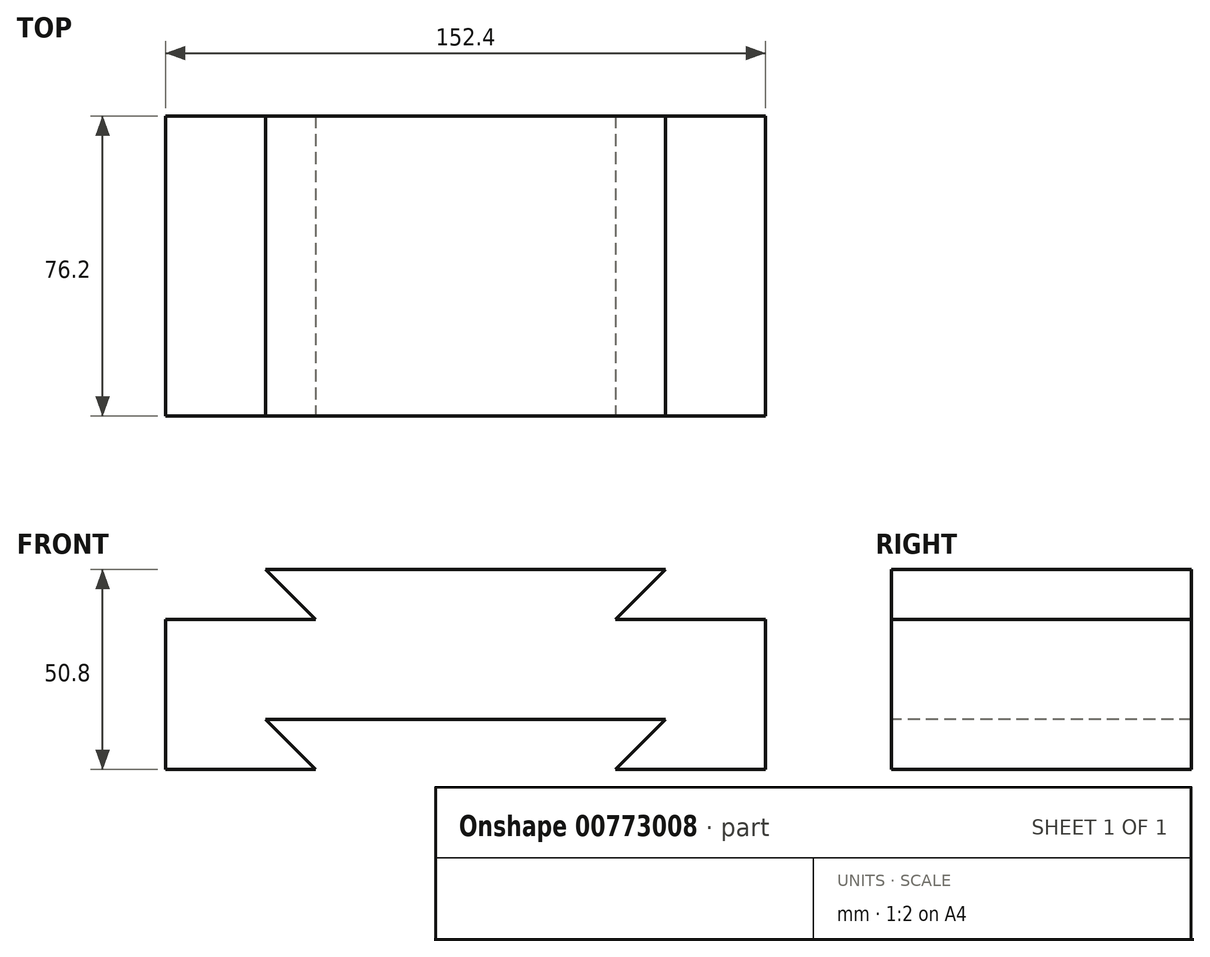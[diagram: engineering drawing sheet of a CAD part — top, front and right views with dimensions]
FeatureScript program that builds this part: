
annotation { "Feature Type Name" : "Feature", "Feature Type Description" : "" }
export const myFeature = defineFeature(function(context is Context, id is Id, definition is map)
    precondition{}
    {
        {
            var Q0;
            Q0=qCreatedBy(makeId("Front.planeOp"),FACE);
            var sketch = newSketch(context, id + "F0", { "sketchPlane" : qUnion([Q0])});
            skLineSegment(sketch, "E0", {"start": v(0, 0) * mm, "end": v(152.4, 0) * mm});
            skLineSegment(sketch, "E1", {"start": v(152.4, 0) * mm, "end": v(152.4, 50.8) * mm});
            skLineSegment(sketch, "E2", {"start": v(152.4, 50.8) * mm, "end": v(0, 50.8) * mm});
            skLineSegment(sketch, "E3", {"start": v(0, 50.8) * mm, "end": v(0, 0) * mm});
            skSolve(sketch);
        }
        {
            var Q0;
            Q0=makeQuery(id+"F0.imprint","IMPRINT",FACE,{"disambiguationData":[TD([[makeQuery(id+"F0.imprint","IMPRINT",EDGE,{"derivedFrom":sQuery(id+"F0.wireOp",EDGE,"E0")}),1.0]])]});
            extrude(context, id + "F1", {"entities" : qUnion([Q0]), "depth" : 76.2 * mm, "offsetDistance" : 25.4 * mm});
        }
        {
            var Q0;
            Q0=makeQuery(id+"F1.opExtrude","CAP_FACE",FACE,{"disambiguationData":[OSD([sQuery(id+"F0.wireOp",EDGE,"E0"),sQuery(id+"F0.wireOp",EDGE,"E1"),sQuery(id+"F0.wireOp",EDGE,"E2"),sQuery(id+"F0.wireOp",EDGE,"E3")])],"isStart":false});
            var sketch = newSketch(context, id + "F2", { "sketchPlane" : qUnion([Q0])});
            skLineSegment(sketch, "E4", {"start": v(0, 50.8) * mm, "end": v(25.4, 50.8) * mm});
            skLineSegment(sketch, "E5", {"start": v(0, 50.8) * mm, "end": v(0, 38.1) * mm});
            skLineSegment(sketch, "E6", {"start": v(0, 38.1) * mm, "end": v(38.1, 38.1) * mm});
            skLineSegment(sketch, "E7", {"start": v(25.4, 50.8) * mm, "end": v(38.1, 38.1) * mm});
            skSolve(sketch);
        }
        {
            var Q0;
            Q0=makeQuery(id+"F2.imprint","IMPRINT",FACE,{"disambiguationData":[TD([[makeQuery(id+"F2.imprint","IMPRINT",EDGE,{"derivedFrom":sQuery(id+"F2.wireOp",EDGE,"E4")}),1.0]])]});
            extrude(context, id + "F3", {"entities" : qUnion([Q0]), "operationType" : NewBodyOperationType.REMOVE, "oppositeDirection" : true, "depth" : 76.2 * mm, "offsetDistance" : 25.4 * mm});
        }
        {
            var Q0;
            Q0=makeQuery(id+"F1.opExtrude","CAP_FACE",FACE,{"disambiguationData":[OSD([sQuery(id+"F0.wireOp",EDGE,"E0"),sQuery(id+"F0.wireOp",EDGE,"E1"),sQuery(id+"F0.wireOp",EDGE,"E2"),sQuery(id+"F0.wireOp",EDGE,"E3")])],"isStart":false});
            var sketch = newSketch(context, id + "F4", { "sketchPlane" : qUnion([Q0])});
            skLineSegment(sketch, "E8", {"start": v(152.4, 50.8) * mm, "end": v(127, 50.8) * mm});
            skLineSegment(sketch, "E9", {"start": v(152.4, 50.8) * mm, "end": v(152.4, 38.1) * mm});
            skLineSegment(sketch, "E10", {"start": v(152.4, 38.1) * mm, "end": v(114.3, 38.1) * mm});
            skLineSegment(sketch, "E11", {"start": v(114.3, 38.1) * mm, "end": v(127, 50.8) * mm});
            skSolve(sketch);
        }
        {
            var Q0;
            Q0=makeQuery(id+"F4.imprint","IMPRINT",FACE,{"disambiguationData":[TD([[makeQuery(id+"F4.imprint","IMPRINT",EDGE,{"derivedFrom":sQuery(id+"F4.wireOp",EDGE,"E8")}),1.0]])]});
            extrude(context, id + "F5", {"entities" : qUnion([Q0]), "operationType" : NewBodyOperationType.REMOVE, "oppositeDirection" : true, "depth" : 76.2 * mm, "offsetDistance" : 25.4 * mm});
        }
        {
            var Q0;
            Q0=makeQuery(id+"F1.opExtrude","CAP_FACE",FACE,{"disambiguationData":[OSD([sQuery(id+"F0.wireOp",EDGE,"E0"),sQuery(id+"F0.wireOp",EDGE,"E1"),sQuery(id+"F0.wireOp",EDGE,"E2"),sQuery(id+"F0.wireOp",EDGE,"E3")])],"isStart":false});
            var sketch = newSketch(context, id + "F6", { "sketchPlane" : qUnion([Q0])});
            skLineSegment(sketch, "E12", {"start": v(0, 0) * mm, "end": v(38.1, 0) * mm});
            skLineSegment(sketch, "E13", {"start": v(0, 0) * mm, "end": v(0, 12.7) * mm});
            skLineSegment(sketch, "E14", {"start": v(0, 12.7) * mm, "end": v(25.4, 12.7) * mm});
            skLineSegment(sketch, "E15", {"start": v(25.4, 12.7) * mm, "end": v(38.1, 0) * mm});
            skLineSegment(sketch, "E16", {"start": v(152.4, 0) * mm, "end": v(114.3, 0) * mm});
            skLineSegment(sketch, "E17", {"start": v(152.4, 0) * mm, "end": v(152.4, 12.7) * mm});
            skLineSegment(sketch, "E18", {"start": v(152.4, 12.7) * mm, "end": v(127, 12.7) * mm});
            skLineSegment(sketch, "E19", {"start": v(127, 12.7) * mm, "end": v(114.3, 0) * mm});
            skLineSegment(sketch, "E20", {"start": v(127, 12.7) * mm, "end": v(25.4, 12.7) * mm});
            skSolve(sketch);
        }
        {
            var Q0;
            {var subQ0=sQuery(id+"F6.wireOp",EDGE,"E15");Q0=makeQuery(id+"F6.imprint","IMPRINT",FACE,{"disambiguationData":[TD([[makeQuery(id+"F6.imprint","IMPRINT",EDGE,{"derivedFrom":subQ0}),1.0]])]});}
            extrude(context, id + "F7", {"entities" : qUnion([Q0]), "operationType" : NewBodyOperationType.REMOVE, "oppositeDirection" : true, "depth" : 76.2 * mm, "offsetDistance" : 25.4 * mm});
        }
    });
